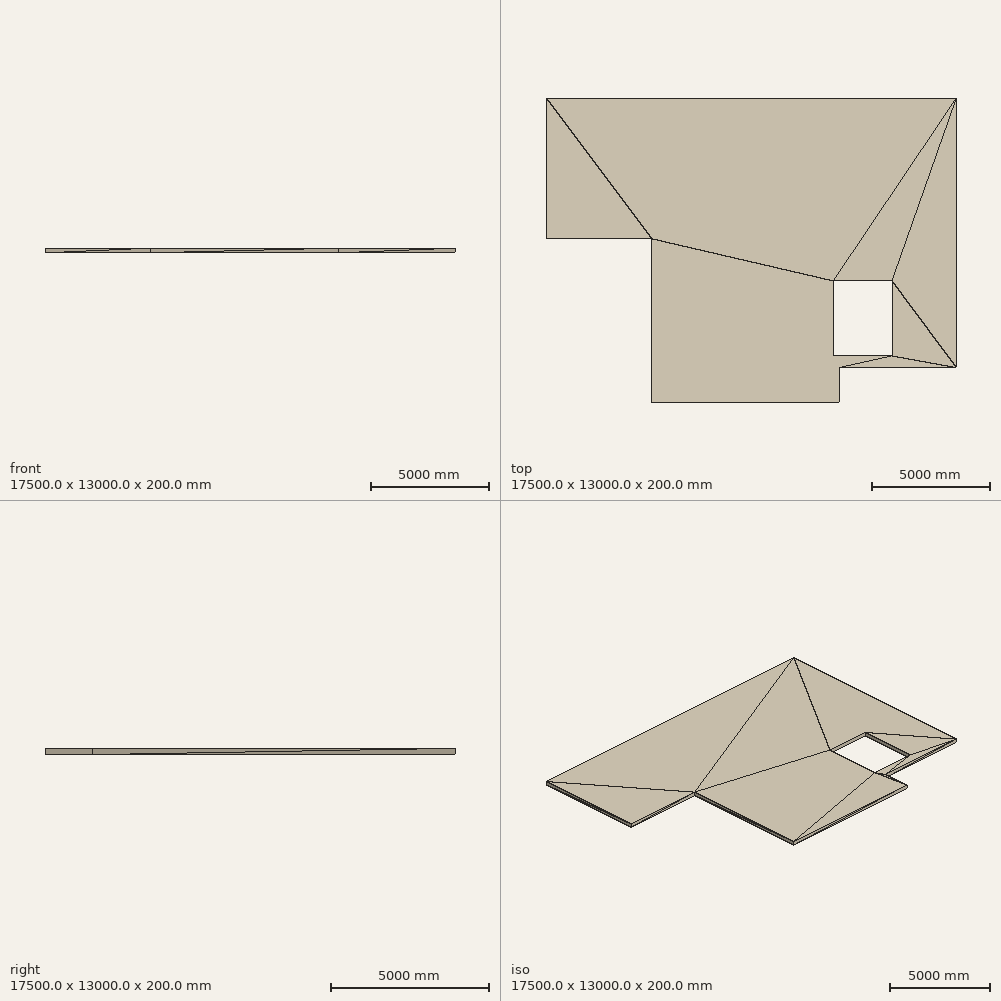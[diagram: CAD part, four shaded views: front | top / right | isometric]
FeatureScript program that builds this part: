
annotation { "Feature Type Name" : "Feature", "Feature Type Description" : "" }
export const myFeature = defineFeature(function(context is Context, id is Id, definition is map)
    precondition{}
    {
        {
            var Q0;
            Q0=qCreatedBy(makeId("Top.planeOp"),FACE);
            var sketch = newSketch(context, id + "F0", { "sketchPlane" : qUnion([Q0])});
            skLineSegment(sketch, "E0", {"start": v(8875, 7625) * mm, "end": v(-8625, 7625) * mm});
            skLineSegment(sketch, "E1", {"start": v(-8625, 7625) * mm, "end": v(-8625, 1625) * mm});
            skLineSegment(sketch, "E2", {"start": v(-8625, 1625) * mm, "end": v(-4125, 1625) * mm});
            skLineSegment(sketch, "E3", {"start": v(-4125, 1625) * mm, "end": v(-4125, -5375) * mm});
            skLineSegment(sketch, "E4", {"start": v(-4125, -5375) * mm, "end": v(3875, -5375) * mm});
            skLineSegment(sketch, "E5", {"start": v(3875, -5375) * mm, "end": v(3875, -3875) * mm});
            skLineSegment(sketch, "E6", {"start": v(3875, -3875) * mm, "end": v(8875, -3875) * mm});
            skLineSegment(sketch, "E7", {"start": v(8875, -3875) * mm, "end": v(8875, 7625) * mm});
            skSolve(sketch);
        }
        {
            var Q0;
            Q0=makeQuery(id+"F0.imprint","IMPRINT",FACE,{"disambiguationData":[TD([[makeQuery(id+"F0.imprint","IMPRINT",EDGE,{"derivedFrom":sQuery(id+"F0.wireOp",EDGE,"E0")}),1.0]])]});
            extrude(context, id + "F1", {"entities" : qUnion([Q0]), "depth" : 200 * mm, "offsetDistance" : 25 * mm});
        }
        {
            var Q0;
            Q0=makeQuery(id+"F1.opExtrude","CAP_FACE",FACE,{"disambiguationData":[OSD([sQuery(id+"F0.wireOp",EDGE,"E0"),sQuery(id+"F0.wireOp",EDGE,"E1"),sQuery(id+"F0.wireOp",EDGE,"E2"),sQuery(id+"F0.wireOp",EDGE,"E3"),sQuery(id+"F0.wireOp",EDGE,"E4"),sQuery(id+"F0.wireOp",EDGE,"E5"),sQuery(id+"F0.wireOp",EDGE,"E6"),sQuery(id+"F0.wireOp",EDGE,"E7")])],"isStart":false});
            var sketch = newSketch(context, id + "F2", { "sketchPlane" : qUnion([Q0])});
            skLineSegment(sketch, "E8.bottom", {"start": v(3625, -3375) * mm, "end": v(6125, -3375) * mm});
            skLineSegment(sketch, "E8.top", {"start": v(3625, -175) * mm, "end": v(6125, -175) * mm});
            skLineSegment(sketch, "E8.left", {"start": v(3625, -3375) * mm, "end": v(3625, -175) * mm});
            skLineSegment(sketch, "E8.right", {"start": v(6125, -3375) * mm, "end": v(6125, -175) * mm});
            skSolve(sketch);
        }
        {
            var Q0;
            Q0 = qSketchRegion(id + "F2", true);
            extrude(context, id + "F3", {"entities" : qUnion([Q0]), "operationType" : NewBodyOperationType.REMOVE, "endBound" : BoundingType.UP_TO_NEXT, "oppositeDirection" : true, "depth" : 25 * mm, "offsetDistance" : 25 * mm});
        }
    });
